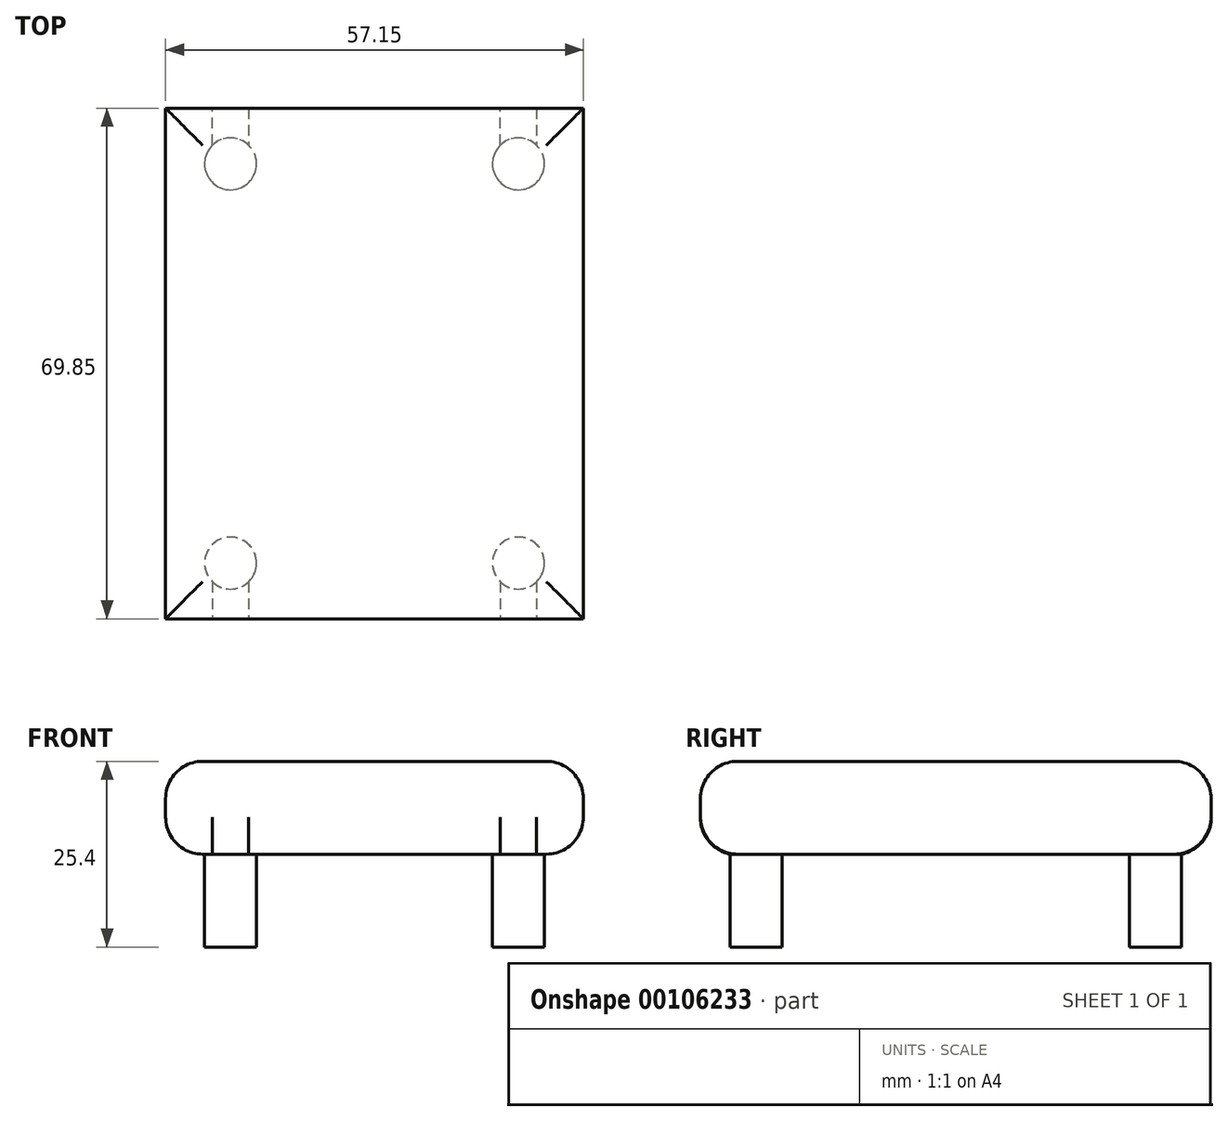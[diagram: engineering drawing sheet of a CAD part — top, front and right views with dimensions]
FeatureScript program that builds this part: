
annotation { "Feature Type Name" : "Feature", "Feature Type Description" : "" }
export const myFeature = defineFeature(function(context is Context, id is Id, definition is map)
    precondition{}
    {
        {
            var Q0;
            Q0=qCreatedBy(makeId("Top.planeOp"),FACE);
            var sketch = newSketch(context, id + "F0", { "sketchPlane" : qUnion([Q0])});
            skLineSegment(sketch, "E0.bottom", {"start": v(-39.83, 49.97) * mm, "end": v(17.32, 49.97) * mm});
            skLineSegment(sketch, "E0.top", {"start": v(-39.83, -19.88) * mm, "end": v(17.32, -19.88) * mm});
            skLineSegment(sketch, "E0.left", {"start": v(-39.83, 49.97) * mm, "end": v(-39.83, -19.88) * mm});
            skLineSegment(sketch, "E0.right", {"start": v(17.32, 49.97) * mm, "end": v(17.32, -19.88) * mm});
            skSolve(sketch);
        }
        {
            var Q0;
            Q0=makeQuery(id+"F0.imprint","IMPRINT",FACE,{"disambiguationData":[TD([[makeQuery(id+"F0.imprint","IMPRINT",EDGE,{"derivedFrom":sQuery(id+"F0.wireOp",EDGE,"E0.bottom")}),-1.0]])]});
            extrude(context, id + "F1", {"entities" : qUnion([Q0]), "depth" : 12.7 * mm});
        }
        {
            var Q0;
            Q0=makeQuery(id+"F1.opExtrude","CAP_FACE",FACE,{"disambiguationData":[OSD([sQuery(id+"F0.wireOp",EDGE,"E0.bottom"),sQuery(id+"F0.wireOp",EDGE,"E0.top"),sQuery(id+"F0.wireOp",EDGE,"E0.left"),sQuery(id+"F0.wireOp",EDGE,"E0.right")])],"isStart":false});
            var sketch = newSketch(context, id + "F2", { "sketchPlane" : qUnion([Q0])});
            skCircle(sketch, "E1", {"center": v(-30.94, 42.35) * mm, "radius": 3.56 * mm});
            skCircle(sketch, "E2", {"center": v(8.43, 42.35) * mm, "radius": 3.56 * mm});
            skCircle(sketch, "E3", {"center": v(-30.94, -12.26) * mm, "radius": 3.56 * mm});
            skCircle(sketch, "E4", {"center": v(8.43, -12.26) * mm, "radius": 3.56 * mm});
            skSolve(sketch);
        }
        {
            var Q0;
            Q0=qSketchRegion(id+"F2",true);
            var Q1;
            Q1=sQuery(id+"F2.wireOp",EDGE,"E4");
            extrude(context, id + "F3", {"entities" : qUnion([Q0]), "operationType" : NewBodyOperationType.ADD, "surfaceEntities" : qUnion([Q1]), "oppositeDirection" : true, "depth" : 25.4 * mm});
        }
        {
            var Q0;
            Q0=makeQuery(id+"F1.opExtrude","CAP_EDGE",EDGE,{"disambiguationData":[OSD([sQuery(id+"F0.wireOp",EDGE,"E0.top")])],"isStart":true});
            var Q1;
            Q1=makeQuery(id+"F1.opExtrude","CAP_EDGE",EDGE,{"disambiguationData":[OSD([sQuery(id+"F0.wireOp",EDGE,"E0.top")])],"isStart":false});
            var Q2;
            Q2=makeQuery(id+"F1.opExtrude","CAP_EDGE",EDGE,{"disambiguationData":[OSD([sQuery(id+"F0.wireOp",EDGE,"E0.right")])],"isStart":true});
            var Q3;
            Q3=makeQuery(id+"F1.opExtrude","CAP_EDGE",EDGE,{"disambiguationData":[OSD([sQuery(id+"F0.wireOp",EDGE,"E0.right")])],"isStart":false});
            var Q4;
            Q4=makeQuery(id+"F1.opExtrude","CAP_EDGE",EDGE,{"disambiguationData":[OSD([sQuery(id+"F0.wireOp",EDGE,"E0.bottom")])],"isStart":false});
            var Q5;
            Q5=makeQuery(id+"F1.opExtrude","CAP_EDGE",EDGE,{"disambiguationData":[OSD([sQuery(id+"F0.wireOp",EDGE,"E0.bottom")])],"isStart":true});
            var Q6;
            Q6=makeQuery(id+"F1.opExtrude","CAP_EDGE",EDGE,{"disambiguationData":[OSD([sQuery(id+"F0.wireOp",EDGE,"E0.left")])],"isStart":false});
            var Q7;
            Q7=makeQuery(id+"F1.opExtrude","CAP_EDGE",EDGE,{"disambiguationData":[OSD([sQuery(id+"F0.wireOp",EDGE,"E0.left")])],"isStart":true});
            fillet(context, id + "F4", {"entities" : qUnion([Q0, Q1, Q2, Q3, Q4, Q5, Q6, Q7]), "radius" : 5.08 * mm, "tangentPropagation" : true, "allowEdgeOverflow" : false});
        }
    });
